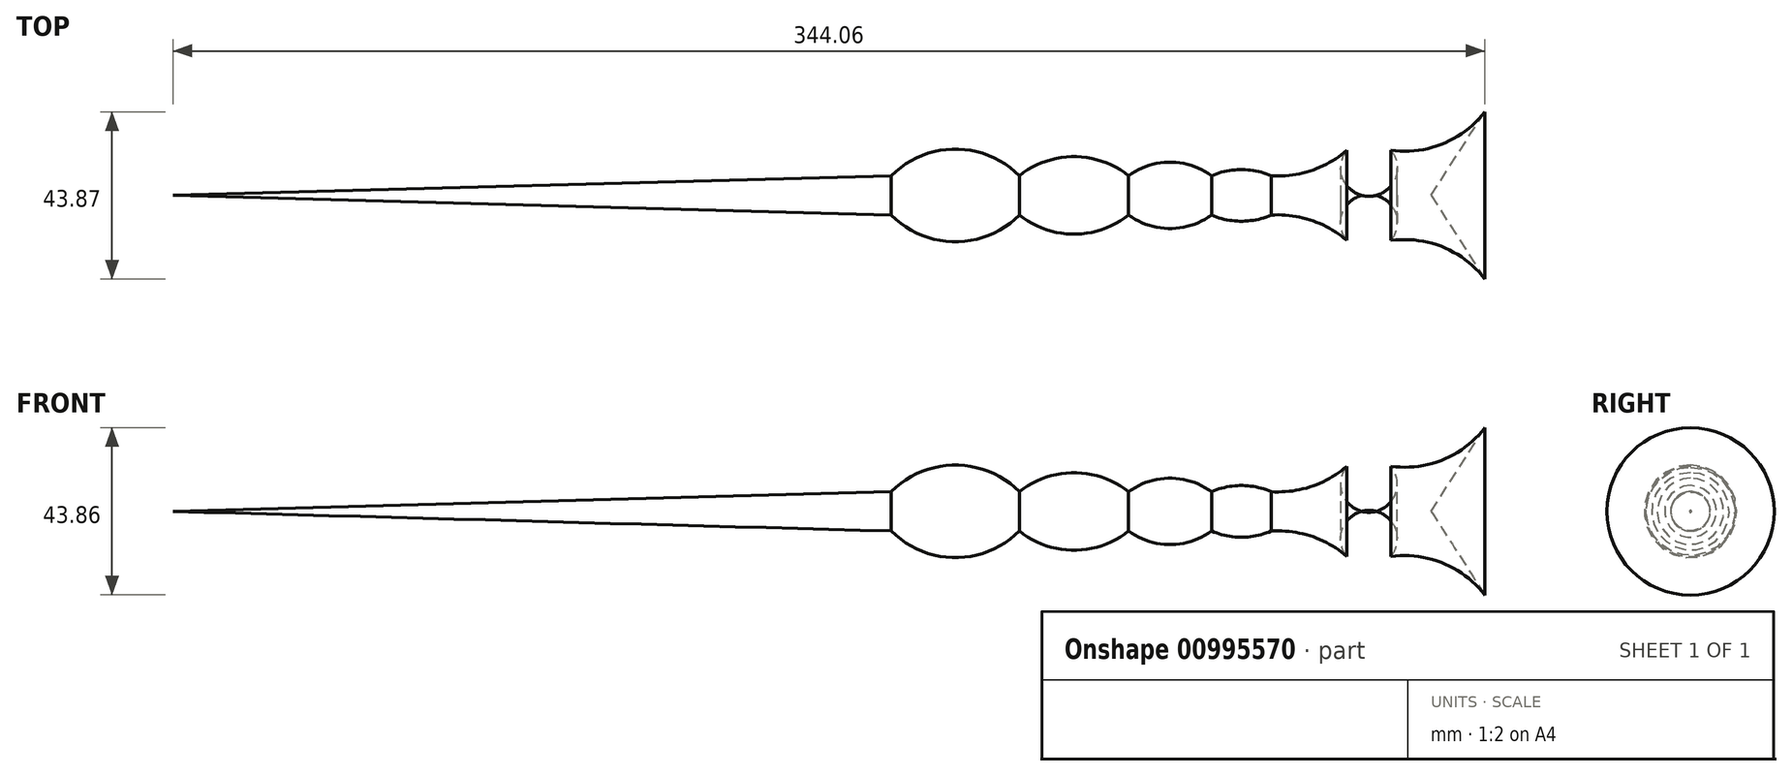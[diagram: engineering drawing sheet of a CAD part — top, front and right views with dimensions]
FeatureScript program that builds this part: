
annotation { "Feature Type Name" : "Feature", "Feature Type Description" : "" }
export const myFeature = defineFeature(function(context is Context, id is Id, definition is map)
    precondition{}
    {
        {
            var Q0;
            Q0=qCreatedBy(makeId("Top.planeOp"),FACE);
            var sketch = newSketch(context, id + "F0", { "sketchPlane" : qUnion([Q0])});
            skLineSegment(sketch, "E0", {"start": v(-154.33, 12.07) * mm, "end": v(182.04, 12.07) * mm});
            skPoint(sketch, "E1.orphan", {"position": v(114.66, 12.07) * mm});
            skArc(sketch, "E2", {"start": v(74.05, 17.23) * mm, "mid": v(57.26, 24.2) * mm, "end": v(40.47, 17.23) * mm});
            skArc(sketch, "E3", {"start": v(102.69, 17.23) * mm, "mid": v(88.37, 22.22) * mm, "end": v(74.05, 17.23) * mm});
            skArc(sketch, "E4", {"start": v(124.46, 17.23) * mm, "mid": v(113.57, 20.76) * mm, "end": v(102.69, 17.23) * mm});
            skArc(sketch, "E5", {"start": v(140.1, 17.23) * mm, "mid": v(132.28, 18.84) * mm, "end": v(124.46, 17.23) * mm});
            skPoint(sketch, "E6.orphan", {"position": v(140.26, 12.07) * mm});
            skArc(sketch, "E7", {"start": v(140.1, 17.23) * mm, "mid": v(150.67, 18.6) * mm, "end": v(159.94, 23.9) * mm});
            skArc(sketch, "E8", {"start": v(171.54, 23.9) * mm, "mid": v(165.74, 26.68) * mm, "end": v(159.94, 23.9) * mm});
            skArc(sketch, "E9", {"start": v(171.54, 23.9) * mm, "mid": v(187.25, 26.6) * mm, "end": v(198.58, 37.8) * mm});
            skLineSegment(sketch, "E10", {"start": v(40.47, 17.23) * mm, "end": v(-147.92, 12.07) * mm});
            skLineSegment(sketch, "E11", {"start": v(182.04, 12.07) * mm, "end": v(198.58, 37.8) * mm});
            skSolve(sketch);
        }
        {
            var Q0;
            Q0=makeQuery(id+"F0.imprint","IMPRINT",FACE,{"disambiguationData":[TD([[makeQuery(id+"F0.imprint","IMPRINT",EDGE,{"derivedFrom":sQuery(id+"F0.wireOp",EDGE,"E2")}),1.0]])]});
            var Q1;
            Q1=sQuery(id+"F0.wireOp",EDGE,"E0");
            revolve(context, id + "F1", {"surfaceOperationType" : NewSurfaceOperationType.NEW, "entities" : qUnion([Q0]), "axis" : qUnion([Q1]), "revolveType" : RevolveType.FULL});
        }
    });
